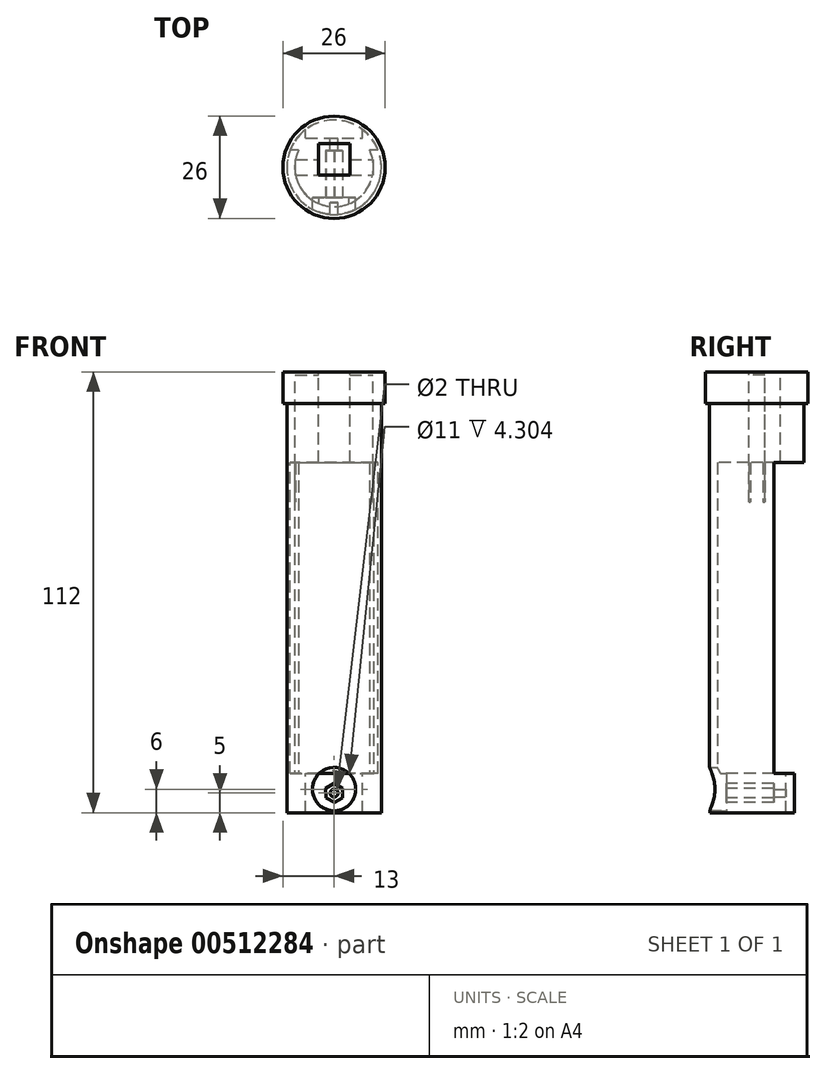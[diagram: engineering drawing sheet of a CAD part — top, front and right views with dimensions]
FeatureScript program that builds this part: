
annotation { "Feature Type Name" : "Feature", "Feature Type Description" : "" }
export const myFeature = defineFeature(function(context is Context, id is Id, definition is map)
    precondition{}
    {
        {
            var Q0;
            Q0=qCreatedBy(makeId("Top.planeOp"),FACE);
            var sketch = newSketch(context, id + "F0", { "sketchPlane" : qUnion([Q0])});
            skCircle(sketch, "E0", {"center": v(0, 0) * mm, "radius": 12 * mm});
            skSolve(sketch);
        }
        {
            var Q0;
            Q0 = qSketchRegion(id + "F0", true);
            extrude(context, id + "F1", {"entities" : qUnion([Q0]), "oppositeDirection" : true, "depth" : 104 * mm, "offsetDistance" : 25 * mm});
        }
        {
            var Q0;
            Q0=makeQuery(id+"F1.opExtrude","CAP_FACE",FACE,{"disambiguationData":[OSD([sQuery(id+"F0.wireOp",EDGE,"E0")])],"isStart":true});
            var sketch = newSketch(context, id + "F2", { "sketchPlane" : qUnion([Q0])});
            skCircle(sketch, "E1", {"center": v(0, 0) * mm, "radius": 13 * mm});
            skSolve(sketch);
        }
        {
            var Q0;
            Q0 = qSketchRegion(id + "F2", true);
            extrude(context, id + "F3", {"entities" : qUnion([Q0]), "operationType" : NewBodyOperationType.ADD, "depth" : 8 * mm, "offsetDistance" : 25 * mm});
        }
        {
            var Q0;
            Q0=qCreatedBy(makeId("Top.planeOp"),FACE);
            var sketch = newSketch(context, id + "F4", { "sketchPlane" : qUnion([Q0])});
            skLineSegment(sketch, "E2", {"start": v(0, -1.7) * mm, "end": v(0, 2.26) * mm, "construction": true});
            skLineSegment(sketch, "E3", {"start": v(-2.5, 0) * mm, "end": v(2.6, 0) * mm, "construction": true});
            skLineSegment(sketch, "E4.bottom", {"start": v(-9.87, 2) * mm, "end": v(-4, 2) * mm});
            skLineSegment(sketch, "E4.top", {"start": v(-9.87, -2) * mm, "end": v(9.87, -2) * mm});
            skLineSegment(sketch, "E4.left", {"start": v(-9.87, 2) * mm, "end": v(-9.87, -2) * mm});
            skLineSegment(sketch, "E4.right", {"start": v(9.88, 2) * mm, "end": v(9.88, -2) * mm});
            skLineSegment(sketch, "E5.bottom", {"start": v(-4, 6) * mm, "end": v(4, 6) * mm});
            skLineSegment(sketch, "E5.left", {"start": v(-4, 6) * mm, "end": v(-4, 2) * mm});
            skLineSegment(sketch, "E5.right", {"start": v(4, 6) * mm, "end": v(4, 2) * mm});
            skLineSegment(sketch, "E6.trimOffspring", {"start": v(4, 2) * mm, "end": v(9.87, 2) * mm});
            skSolve(sketch);
        }
        {
            var Q0;
            Q0 = qSketchRegion(id + "F4", true);
            extrude(context, id + "F5", {"entities" : qUnion([Q0]), "operationType" : NewBodyOperationType.REMOVE, "endBound" : BoundingType.SYMMETRIC, "oppositeDirection" : true, "depth" : 50 * mm, "offsetDistance" : 25 * mm});
        }
        {
            var Q0;
            Q0=makeQuery(id+"F1.opExtrude","CAP_FACE",FACE,{"disambiguationData":[OSD([sQuery(id+"F0.wireOp",EDGE,"E0")])],"isStart":false});
            cPlane(context, id + "F6", {"entities" : qUnion([Q0]), "cplaneType" : CPlaneType.OFFSET, "offset" : 10 * mm, "oppositeDirection" : true, "width" : 150 * mm, "height" : 150 * mm});
        }
        {
            var Q0;
            Q0=qCreatedBy(id+"F6.planeOp",FACE);
            var sketch = newSketch(context, id + "F7", { "sketchPlane" : qUnion([Q0])});
            skArc(sketch, "E7", {"start": v(9, -4.36) * mm, "mid": v(0, 10) * mm, "end": v(-9, -4.36) * mm});
            skLineSegment(sketch, "E8.right", {"start": v(9, -4.36) * mm, "end": v(9, -4.36) * mm});
            skLineSegment(sketch, "E9", {"start": v(0, 0) * mm, "end": v(0, -15.45) * mm, "construction": true});
            skLineSegment(sketch, "E10", {"start": v(-9, -4.36) * mm, "end": v(-12.25, -4.36) * mm});
            skLineSegment(sketch, "E11", {"start": v(12.25, -4.36) * mm, "end": v(9, -4.36) * mm});
            skArc(sketch, "E12.0", {"start": v(-12.25, -4.36) * mm, "mid": v(0, -13) * mm, "end": v(12.25, -4.36) * mm});
            skPoint(sketch, "E13.orphan", {"position": v(16, -4.36) * mm});
            skSolve(sketch);
        }
        {
            var Q0;
            Q0 = qSketchRegion(id + "F7", true);
            extrude(context, id + "F8", {"entities" : qUnion([Q0]), "operationType" : NewBodyOperationType.REMOVE, "oppositeDirection" : true, "depth" : 79 * mm, "offsetDistance" : 25 * mm});
        }
        {
            var Q0;
            Q0=qCreatedBy(id+"F6.planeOp",FACE);
            var sketch = newSketch(context, id + "F9", { "sketchPlane" : qUnion([Q0])});
            skLineSegment(sketch, "E14.0", {"start": v(-7.2, -7.4) * mm, "end": v(-7.2, -10.82) * mm});
            skLineSegment(sketch, "E15.0", {"start": v(7.2, -7.4) * mm, "end": v(7.2, -10.82) * mm});
            skLineSegment(sketch, "E16", {"start": v(-7.2, -7.4) * mm, "end": v(7.2, -7.4) * mm});
            skArc(sketch, "E17.0", {"start": v(-7.2, -10.82) * mm, "mid": v(0, -13) * mm, "end": v(7.2, -10.82) * mm});
            skPoint(sketch, "E18.orphan", {"position": v(-7.2, -9.6) * mm});
            skPoint(sketch, "E19.orphan", {"position": v(7.2, -9.6) * mm});
            skSolve(sketch);
        }
        {
            var Q0;
            Q0 = qSketchRegion(id + "F9", true);
            extrude(context, id + "F10", {"entities" : qUnion([Q0]), "operationType" : NewBodyOperationType.REMOVE, "endBound" : BoundingType.THROUGH_ALL, "depth" : 25 * mm, "offsetDistance" : 25 * mm});
        }
        {
            var Q0;
            Q0=makeQuery(id+"F1.opExtrude","CAP_FACE",FACE,{"disambiguationData":[OSD([sQuery(id+"F0.wireOp",EDGE,"E0")])],"isStart":false});
            var sketch = newSketch(context, id + "F11", { "sketchPlane" : qUnion([Q0])});
            skLineSegment(sketch, "E20", {"start": v(0, 0) * mm, "end": v(0, 10.17) * mm, "construction": true});
            skLineSegment(sketch, "E21.bottom", {"start": v(-1, 14) * mm, "end": v(1, 14) * mm});
            skLineSegment(sketch, "E21.top", {"start": v(-1, 9) * mm, "end": v(1, 9) * mm});
            skLineSegment(sketch, "E21.left", {"start": v(-1, 14) * mm, "end": v(-1, 9) * mm});
            skLineSegment(sketch, "E21.right", {"start": v(1, 14) * mm, "end": v(1, 9) * mm});
            skSolve(sketch);
        }
        {
            var Q0;
            Q0 = qSketchRegion(id + "F11", true);
            extrude(context, id + "F12", {"entities" : qUnion([Q0]), "operationType" : NewBodyOperationType.REMOVE, "oppositeDirection" : true, "depth" : 6 * mm, "offsetDistance" : 25 * mm});
        }
        {
            var Q0;
            Q0=makeQuery(id+"F12.boolean.opBoolean","COPY",FACE,{"derivedFrom":makeQuery(id+"F12.opExtrude","SWEPT_FACE",FACE,{"disambiguationData":[OSD([sQuery(id+"F11.wireOp",EDGE,"E21.top")])]})});
            cPlane(context, id + "F13", {"entities" : qUnion([Q0]), "cplaneType" : CPlaneType.OFFSET, "offset" : 1.3 * mm, "oppositeDirection" : true, "width" : 150 * mm, "height" : 150 * mm});
        }
        {
            var Q0;
            Q0=qCreatedBy(id+"F13.planeOp",FACE);
            var sketch = newSketch(context, id + "F14", { "sketchPlane" : qUnion([Q0])});
            skCircle(sketch, "E22", {"center": v(0, -98) * mm, "radius": 5.5 * mm});
            skSolve(sketch);
        }
        {
            var Q0;
            Q0 = qSketchRegion(id + "F14", true);
            extrude(context, id + "F15", {"entities" : qUnion([Q0]), "operationType" : NewBodyOperationType.REMOVE, "endBound" : BoundingType.THROUGH_ALL, "depth" : 2 * mm, "offsetDistance" : 25 * mm});
        }
        {
            var Q0;
            Q0=makeQuery(id+"F3.opExtrude","CAP_FACE",FACE,{"disambiguationData":[OSD([sQuery(id+"F2.wireOp",EDGE,"E1")])],"isStart":false});
            var sketch = newSketch(context, id + "F16", { "sketchPlane" : qUnion([Q0])});
            skLineSegment(sketch, "E23.bottom", {"start": v(-4, 2) * mm, "end": v(-9.87, 2) * mm});
            skLineSegment(sketch, "E23.top", {"start": v(-4, -2) * mm, "end": v(-9.87, -2) * mm});
            skLineSegment(sketch, "E23.left", {"start": v(-4, 2) * mm, "end": v(-4, -2) * mm});
            skLineSegment(sketch, "E23.right", {"start": v(-9.87, 2) * mm, "end": v(-9.87, -2) * mm});
            skLineSegment(sketch, "E24.bottom", {"start": v(4, 2) * mm, "end": v(9.88, 2) * mm});
            skLineSegment(sketch, "E24.top", {"start": v(4, -2) * mm, "end": v(9.88, -2) * mm});
            skLineSegment(sketch, "E24.left", {"start": v(4, 2) * mm, "end": v(4, -2) * mm});
            skLineSegment(sketch, "E24.right", {"start": v(9.88, 2) * mm, "end": v(9.88, -2) * mm});
            skSolve(sketch);
        }
        {
            var Q0;
            Q0 = qSketchRegion(id + "F16", true);
            extrude(context, id + "F17", {"entities" : qUnion([Q0]), "operationType" : NewBodyOperationType.ADD, "oppositeDirection" : true, "depth" : .8 * mm, "offsetDistance" : 25 * mm});
        }
        {
            var Q0;
            Q0=makeQuery(id+"F10.boolean.opBoolean","COPY",FACE,{"derivedFrom":makeQuery(id+"F10.opExtrude","SWEPT_FACE",FACE,{"disambiguationData":[OSD([sQuery(id+"F9.wireOp",EDGE,"E16")])]})});
            var sketch = newSketch(context, id + "F18", { "sketchPlane" : qUnion([Q0])});
            skLineSegment(sketch, "E25.0", {"start": v(7.2, -94) * mm, "end": v(-7.2, -94) * mm, "construction": true});
            skLineSegment(sketch, "E26.0", {"start": v(7.2, -104) * mm, "end": v(-7.2, -104) * mm, "construction": true});
            skLineSegment(sketch, "E27", {"start": v(0, -94) * mm, "end": v(0, -104) * mm, "construction": true});
            skCircle(sketch, "E28", {"center": v(0, -99) * mm, "radius": 1 * mm});
            skSolve(sketch);
        }
        {
            var Q0;
            Q0 = qSketchRegion(id + "F18", true);
            extrude(context, id + "F19", {"entities" : qUnion([Q0]), "operationType" : NewBodyOperationType.REMOVE, "endBound" : BoundingType.THROUGH_ALL, "oppositeDirection" : true, "depth" : 25 * mm, "offsetDistance" : 25 * mm});
        }
        {
            var Q0;
            Q0=makeQuery(id+"F15.boolean.opBoolean","COPY",FACE,{"derivedFrom":makeQuery(id+"F15.opExtrude","CAP_FACE",FACE,{"disambiguationData":[OSD([sQuery(id+"F14.wireOp",EDGE,"E22")])],"isStart":true})});
            var sketch = newSketch(context, id + "F20", { "sketchPlane" : qUnion([Q0])});
            skCircle(sketch, "E29.cCircle", {"center": v(0, -99) * mm, "radius": 2.1 * mm, "construction": true});
            skLineSegment(sketch, "E29.0", {"start": v(2.12, -100.18) * mm, "end": v(0.04, -101.42) * mm});
            skLineSegment(sketch, "E29.1", {"start": v(0.04, -101.42) * mm, "end": v(-2.08, -100.25) * mm});
            skLineSegment(sketch, "E29.2", {"start": v(-2.08, -100.25) * mm, "end": v(-2.12, -97.82) * mm});
            skLineSegment(sketch, "E29.3", {"start": v(-2.12, -97.82) * mm, "end": v(-0.04, -96.58) * mm});
            skLineSegment(sketch, "E29.4", {"start": v(-0.04, -96.58) * mm, "end": v(2.08, -97.75) * mm});
            skLineSegment(sketch, "E29.5", {"start": v(2.08, -97.75) * mm, "end": v(2.12, -100.18) * mm});
            skPoint(sketch, "E29.0.midPoint", {"position": v(1.08, -100.8) * mm});
            skSolve(sketch);
        }
        {
            var Q0;
            Q0 = qSketchRegion(id + "F20", true);
            extrude(context, id + "F21", {"entities" : qUnion([Q0]), "operationType" : NewBodyOperationType.REMOVE, "oppositeDirection" : true, "depth" : 12 * mm, "offsetDistance" : 25 * mm});
        }
    });
